# Revit family: KCV_83in
name_source: partatom
category: Mechanical Equipment
units: mm (PartAtom-declared; Revit-internal decimal feet)

## family parameters
Always vertical = Yes
Classification = None
Cut with Voids When Loaded = No
Maintain Annotation Orientation = No
OmniClass Number = 23.75.70.17.17
OmniClass Title = Radiation Panels
Part Type = Normal
Room Calculation Point = Yes
Round Connector Dimension = Use Diameter
Shared = No
Work Plane-Based = Yes

## types (6) — shared parameters
BIMobject Category = Heaters
Default Elevation = 6' - 0"
Depth = 0' 3-7/8"
Description = Cove Heater, alCove® KCV Series
Design Country = United States
Electrical Connection Type = Hardwired
Electrical KO Locations = Back Only
Electrical KO Sizes = 1/2"
Export Type to IFC As = IfcSpaceHeaterType
Frequency = 60 Hz
Height = 0' 4"
Length = 6' - 11"
Manufacturer = King Electrical Manufacturing Company
Manufacturer Country = United States
Material Extrusion = Aluminum
Material Main = Metal
Minimum Clearance Draperies Above = 3' 0"
Minimum Clearance Draperies Below = 0' 2-1/2"
Minimum Clearance Drop Ceiling = 0' 6"
Minimum Clearance Drywall Ceiling = 0' 2-1/2"
Minimum Clearance From Floor = 6' 0"
Minimum Clearance Sides = 0' 4"
Minumum Clearance Front = 3' 0"
Omniclass Number = 23.75.70.17.17
Phase = 1
Product Family = HVAC
Product Group = Heaters
Revision Date = 04/08/26
Revision Description = Copied KCV_24in. Changed model from KCV_24in to KCV_34in. Set up parameters
Revision Letter = -
Type IFC Predefined Type = RADIATOR
UL Category (CNN) = 827J
UL File Number = E41422
UL Listing = UL 2021
UNSPSC Code = 40101801
URL = https://king-electric.com
URL Catalog Page = https://king-electric.com
URL How To Size Heater = https://king-electric.com
URL Installation Instructions = https://king-electric.com
URL Product Page = https://king-electric.com
URL Quote Submittal = https://king-electric.com
Weight = 15.3 Lbs.
Width = 6' 11"
YouTube Clip - Benefits = https://king-electric.com
YouTube Clip - Installation = https://www.youtube.com

## per-type parameters (varying)
| type | Amperage | BTU/hr | Material Color | Voltage | Wattage |
| KCV1210-W | 7.80 A | 3,000.00 BTU/hr | White | 120.00 V | 935.00 W |
| KCV1210-A | 7.80 A | 3,000.00 BTU/hr | Almond | 120.00 V | 935.00 W |
| KCV2010-W | 4.50 A | 3,000.00 BTU/hr | White | 208.00 V | 935.00 W |
| KCV2010-A | 4.50 A | 3,000.00 BTU/hr | Almond | 208.00 V | 935.00 W |
| KCV2410-W | 3.90 / 3.40 A | 2,000 / 3,000.00 BTU/hr | White | 208.00 / 240.00 V | 701.00 / 935.00 W |
| KCV2410-A | 3.90 / 3.40 A | 2,000 / 3,000.00 BTU/hr | Almond | 208.00 / 240.00 V | 701.00 / 935.00 W |

note: column(s) folded — value = type name in every type: Model

## geometry (parser evidence)
native form markers: Sweep x11
no freeform markers — native parametric forms only
